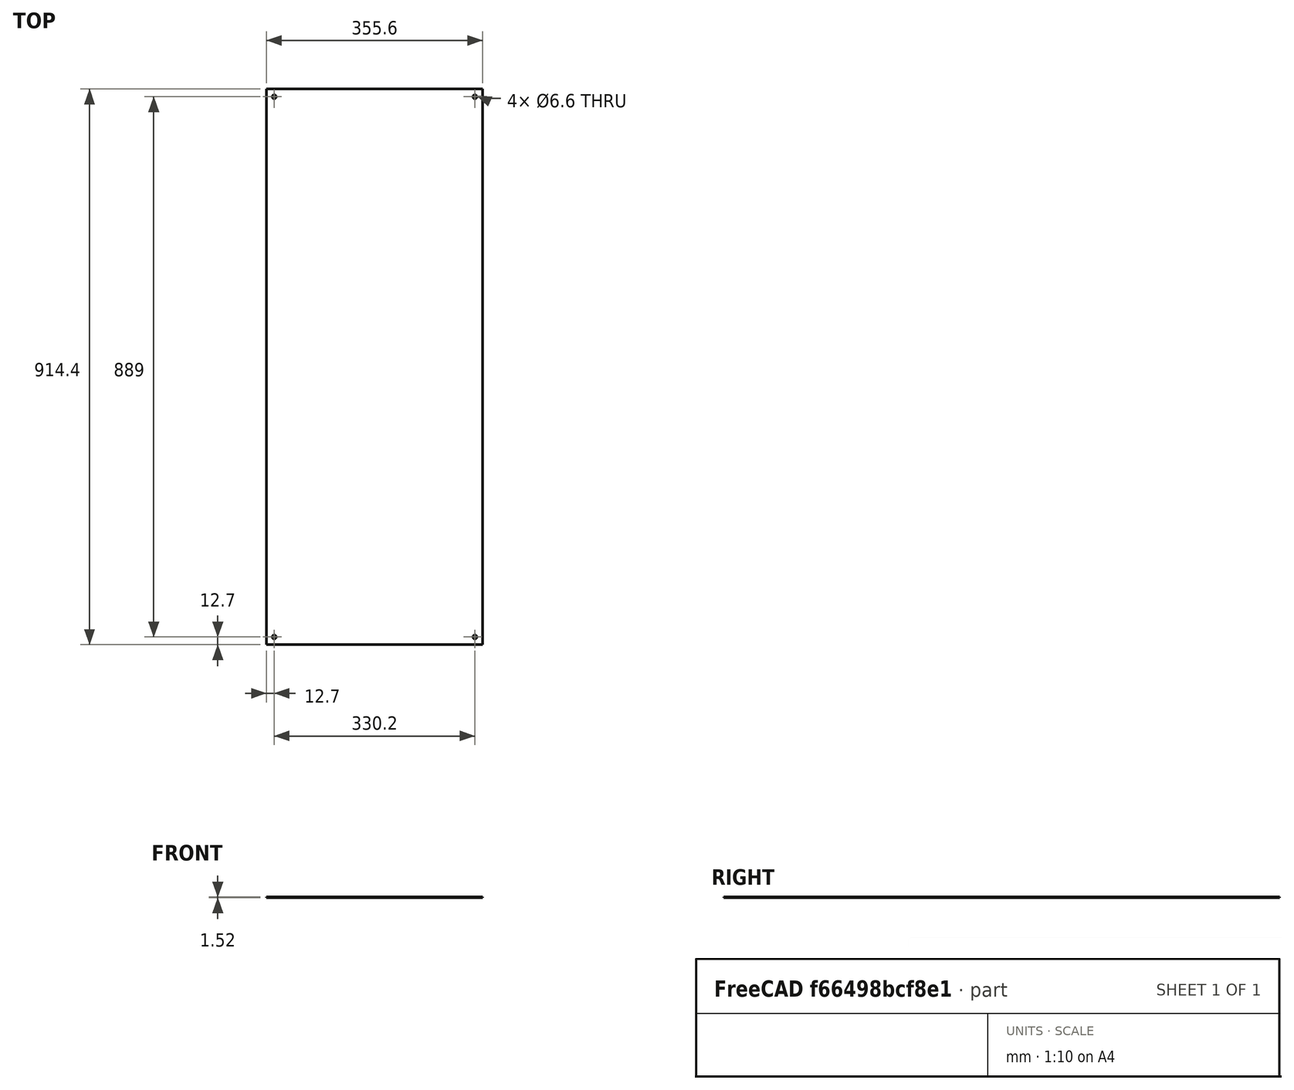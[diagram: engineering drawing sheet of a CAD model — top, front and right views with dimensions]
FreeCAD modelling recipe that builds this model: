
FCSTD DOCUMENT  (FreeCAD 0.21R33694 (Git))
Label: Steel_Sheet_14inx36inx16ga
License: All rights reserved
LicenseURL: http://en.wikipedia.org/wiki/All_rights_reserved
objects: Sketcher::SketchObject×1, PartDesign::Pad×1, PartDesign::Body×1
note: 4 computed .brp shape members not serialized (recipe doc carries the construction recipe); baked Part::Feature solids carry a one-line shape summary decoded from their .brp

FEATURE [Sketcher::SketchObject] Sketch
  FullyConstrained = true
  MapMode = 5
  Support = -> [XY_Plane]
  sketch-geometry (16):
    g0: LineSegment StartX=-177.8 StartY=457.2 StartZ=0 EndX=177.8 EndY=457.2 EndZ=0
    g1: LineSegment StartX=177.8 StartY=457.2 StartZ=0 EndX=177.8 EndY=-457.2 EndZ=0
    g2: LineSegment StartX=177.8 StartY=-457.2 StartZ=0 EndX=-177.8 EndY=-457.2 EndZ=0
    g3: LineSegment StartX=-177.8 StartY=-457.2 StartZ=0 EndX=-177.8 EndY=457.2 EndZ=0
    g4: LineSegment StartX=177.8 StartY=457.2 StartZ=0 EndX=165.1 EndY=457.2 EndZ=0
    g5: LineSegment StartX=165.1 StartY=457.2 StartZ=0 EndX=165.1 EndY=444.5 EndZ=0
    g6: Circle CenterX=165.1 CenterY=444.5 CenterZ=0 NormalX=0 NormalY=0 NormalZ=1 AngleXU=0 Radius=3.3
    g7: LineSegment StartX=-177.8 StartY=457.2 StartZ=0 EndX=-165.1 EndY=457.2 EndZ=0
    g8: LineSegment StartX=-165.1 StartY=457.2 StartZ=0 EndX=-165.1 EndY=444.5 EndZ=0
    g9: Circle CenterX=-165.1 CenterY=444.5 CenterZ=0 NormalX=0 NormalY=0 NormalZ=1 AngleXU=0 Radius=3.3
    g10: LineSegment StartX=-177.8 StartY=-457.2 StartZ=0 EndX=-165.1 EndY=-457.2 EndZ=0
    g11: LineSegment StartX=-165.1 StartY=-457.2 StartZ=0 EndX=-165.1 EndY=-444.5 EndZ=0
    g12: Circle CenterX=-165.1 CenterY=-444.5 CenterZ=0 NormalX=0 NormalY=0 NormalZ=1 AngleXU=0 Radius=3.3
    g13: LineSegment StartX=177.8 StartY=-457.2 StartZ=0 EndX=165.1 EndY=-457.2 EndZ=0
    g14: LineSegment StartX=165.1 StartY=-457.2 StartZ=0 EndX=165.1 EndY=-444.5 EndZ=0
    g15: Circle CenterX=165.1 CenterY=-444.5 CenterZ=0 NormalX=0 NormalY=0 NormalZ=1 AngleXU=0 Radius=3.3
  constraints (43):
    c: Coincident(g0,g1)
    c: Coincident(g1,g2)
    c: Coincident(g2,g3)
    c: Coincident(g3,g0)
    c: Horizontal(g0)
    c: Horizontal(g2)
    c: Vertical(g1)
    c: Vertical(g3)
    c: Symmetric(g2,g0,g-1)
    c: DistanceX(g0,g0) = 355.6
    c: Coincident(g4,g5)
    c: Horizontal(g4)
    c: Vertical(g5)
    c: Coincident(g4,g0)
    c: DistanceX(g4,g4) = 12.7
    c: Coincident(g6,g5)
    c: Coincident(g7,g8)
    c: Horizontal(g7)
    c: Vertical(g8)
    c: Coincident(g7,g0)
    c: Coincident(g9,g8)
    c: Coincident(g10,g11)
    c: Horizontal(g10)
    c: Vertical(g11)
    c: Coincident(g10,g2)
    c: Coincident(g12,g11)
    c: Coincident(g13,g14)
    c: Horizontal(g13)
    c: Vertical(g14)
    c: Coincident(g13,g1)
    c: Coincident(g15,g14)
    c: DistanceY(g1,g1) = 914.4
    c: Horizontal(g9,g6)
    c: Horizontal(g12,g15)
    c: Vertical(g6,g15)
    c: Vertical(g12,g9)
    c: DistanceX(g7,g7) = 12.7
    c: DistanceY(g8,g8) = 12.7
    c: Diameter(g9) = 6.6
    c: Equal(g6,g9)
    c: Equal(g9,g12)
    c: Equal(g12,g15)
    c: DistanceY(g11,g11) = 12.7
FEATURE [PartDesign::Pad] Pad
  Direction = (0,0,1)
  Length = 1.519
  Length2 = 10
  Profile = -> Sketch
  ReferenceAxis = -> Sketch [N_Axis]
  Type = 0
FEATURE [PartDesign::Body] Body
  Group = -> [Sketch,Pad]
  Origin = -> Origin
  Tip = -> Pad
